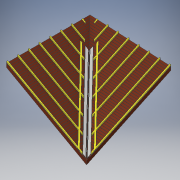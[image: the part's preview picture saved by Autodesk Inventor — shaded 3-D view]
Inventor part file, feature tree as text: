
AUTODESK INVENTOR PART (.ipt)
format: ipt  version: 2019 (Build 230136000, 136)  size: 3,039,232 bytes
history: native  units: in
note: dims shown in document units (in); Inventor stores cm internally (conversion verified against a paired STEP export)
features: plane x11, sketch x10, extrude x6, mirror x5, sweep x1
ambient origin geometry x8: Origin, YZ Plane, XZ Plane, XY Plane, X Axis, Y Axis, Z Axis, Center Point
bodies: Solid1 (feature_tree)
feature tree (33):
  sketch  "Sketch1"  dims[d0=236.2205in d1=236.2205in]
  sketch  "Sketch2"  dims[d2=0.1924in d3=0.1993in]
  plane  "Work Plane1"
  plane  "Work Plane2"
  plane  "Work Plane5"
  extrude  "Extrusion1"  Depth=236.2205in
  mirror  "Mirror1"
  plane  "Work Plane6"
  plane  "Work Plane7"
  sketch  "Sketch4"  dims[d4=90.0deg d5=90.0deg]
  extrude  "Extrusion2"  Depth=0.1993in
  mirror  "Mirror2"
  plane  "Work Plane14"
  extrude  "Extrusion3"  TaperAngle=90.0deg  [1 undecoded]
  mirror  "Mirror3"
  plane  "Work Plane8"
  plane  "Work Plane9"
  sketch  "Sketch6"  dims[d6=4.7244in d7=0.9843in]
  plane  "Work Plane12"
  extrude  "Extrusion4"  Depth=0.9843in
  mirror  "Mirror4"
  extrude  "Extrusion5"  Depth=5.1181in
  mirror  "Mirror5"
  sketch  "Sketch9"  dims[d19=3.937in d20=0.0in]
  sweep  "Sweep1"
  sketch  "Sketch10"  dims[d21=3.3746in d23=27.5591in d24=0.3937in d26=1.0in]
  extrude  "Extrusion7"  TaperAngle=0.0deg  [1 undecoded]
  plane  "Work Plane3"
  plane  "Work Plane4"
  sketch  "Sketch7"  dims[d8=1.0in d9=0.0in d10=18.1708in d12=5.1181in d13=0.3937in d15=1.0in]
  sketch  "Sketch8"  dims[d17=90.0deg d18=7.874in]
  sketch  "3D Sketch1"
  sketch  "Sketch11"  dims[d28=1.0in d29=0.0in d33=3.1496in d34=0.3937in d35=0.3937in d36=0.9843in d37=1.0in d38=0.0in d39=3.3746in d41=27.5591in d42=0.3937in d44=1.0in d46=90.0deg d47=90.0deg d49=90.0deg d53=3.1496in d54=0.3937in d55=1.5748in d56=236.2205in d57=0.0in d59=0.7874in d61=7.874in d62=0.3937in d64=1.0in d66=7.874in d67=2.7559in d68=2.3622in d69=0.1969in d70=3.3746in d72=27.5591in d73=0.3937in d75=1.0in d77=2.3622in d78=2.7559in d79=0.1969in d88=1.1811in d89=2.7559in d90=20.5618in d91=1.0in d92=0.0in d93=7.874in d95=11.811in d96=0.3937in d98=1.0in d100=0.9843in d104=5.9055in d105=0.0in d106=3.937in d108=0.9843in d111=6.6929in d112=0.9449in d113=6.6929in d114=0.7874in d115=0.0in d116=0.0in d117=15.748in d118=19.685in d123=1.0in d124=0.0in d125=4.3307in d127=9.8425in]
note: 2 required parameter values undecoded (feature->parameter linkage not recoverable at this tier; creation-order binding heuristic only, values carry confidence <= 0.55)
